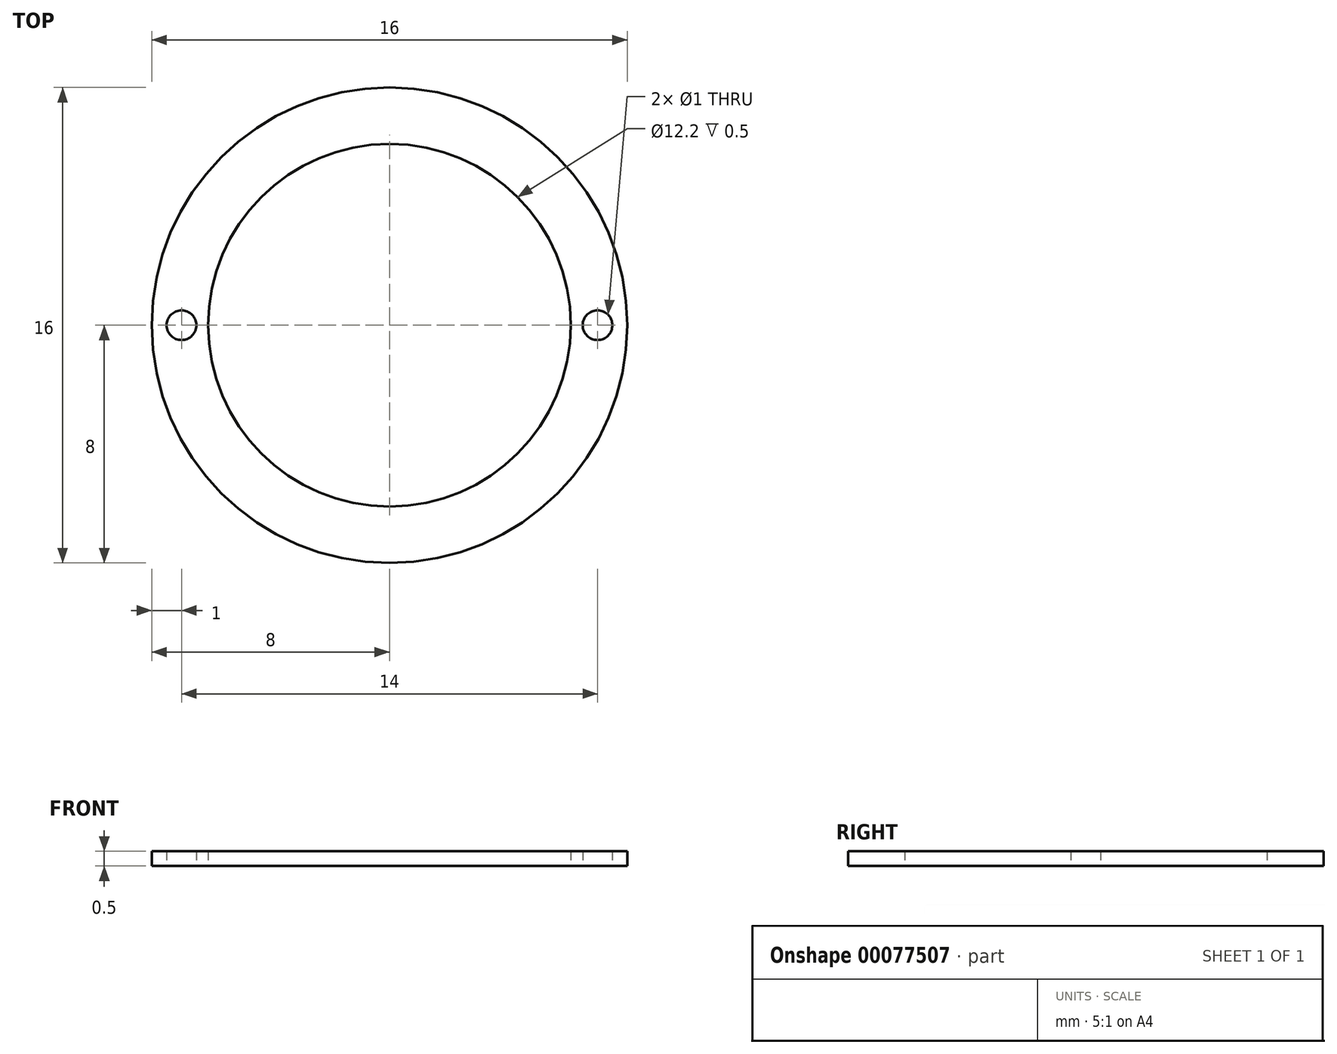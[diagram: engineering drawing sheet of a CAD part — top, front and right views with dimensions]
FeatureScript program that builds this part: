
annotation { "Feature Type Name" : "Feature", "Feature Type Description" : "" }
export const myFeature = defineFeature(function(context is Context, id is Id, definition is map)
    precondition{}
    {
        {
            var Q0;
            Q0=qCreatedBy(makeId("Top.planeOp"),FACE);
            var sketch = newSketch(context, id + "F0", { "sketchPlane" : qUnion([Q0])});
            skCircle(sketch, "E0", {"center": v(0, 0) * mm, "radius": 8 * mm});
            skCircle(sketch, "E1", {"center": v(0, 0) * mm, "radius": 6.1 * mm});
            skCircle(sketch, "E2", {"center": v(0, 0) * mm, "radius": 7 * mm, "construction": true});
            skCircle(sketch, "E3", {"center": v(7, 0) * mm, "radius": 0.5 * mm});
            skCircle(sketch, "E4", {"center": v(-7, 0) * mm, "radius": 0.5 * mm});
            skSolve(sketch);
        }
        {
            var Q0;
            Q0=makeQuery(id+"F0.imprint","IMPRINT",FACE,{"disambiguationData":[TD([[makeQuery(id+"F0.imprint","IMPRINT",EDGE,{"derivedFrom":sQuery(id+"F0.wireOp",EDGE,"E0")}),1.0]])]});
            extrude(context, id + "F1", {"entities" : qUnion([Q0]), "depth" : 0.5 * mm});
        }
    });
